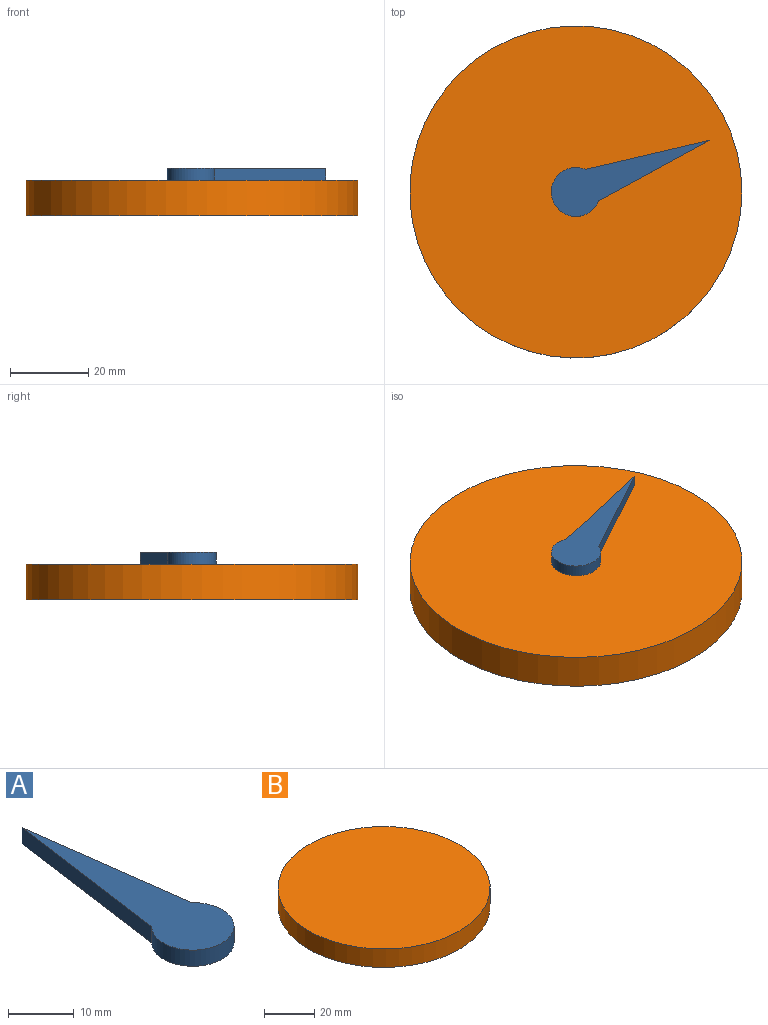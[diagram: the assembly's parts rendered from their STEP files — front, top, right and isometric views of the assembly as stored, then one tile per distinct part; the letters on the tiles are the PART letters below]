
ASSEMBLY  parts=2 mates=1
PART A: 5 faces, bbox 12.5x42.9x3 mm
  f0: cylinder r=6.24mm len=12.49mm, axis (0,0,-1), area 88.7mm2, adj f1,f2,f3,f4
  f1: plane 32.03x4.24mm, normal (0.99,0.13,0), area 96.9mm2, adj f0,f2,f3,f4
  f2: plane 32.27x4.48mm, normal (-0.99,0.14,0), area 97.7mm2, adj f0,f1,f3,f4
  f3: plane 42.87x12.49mm, normal (0,0,1), area 251.9mm2, adj f0,f1,f2
  f4: plane 42.87x12.49mm, normal (0,0,-1), area 251.9mm2, adj f0,f1,f2
PART B: 3 faces, bbox 84.6x84.6x9 mm
  f0: cylinder r=42.32mm len=84.63mm, axis (0,0,-1), area 2392.9mm2, adj f1,f2
  f1: plane 84.63x84.63mm, normal (0,0,1), area 5625.6mm2, adj f0
  f2: plane 84.63x84.63mm, normal (0,0,-1), area 5625.6mm2, adj f0
PLACE A rot(axis=(0,0,-1),68.9deg) t=(0,0,0)mm
PLACE B at identity fixed
MATE revolute B.f0 <-> A.f0  axis (0,0,1) through (0,0,9)mm
